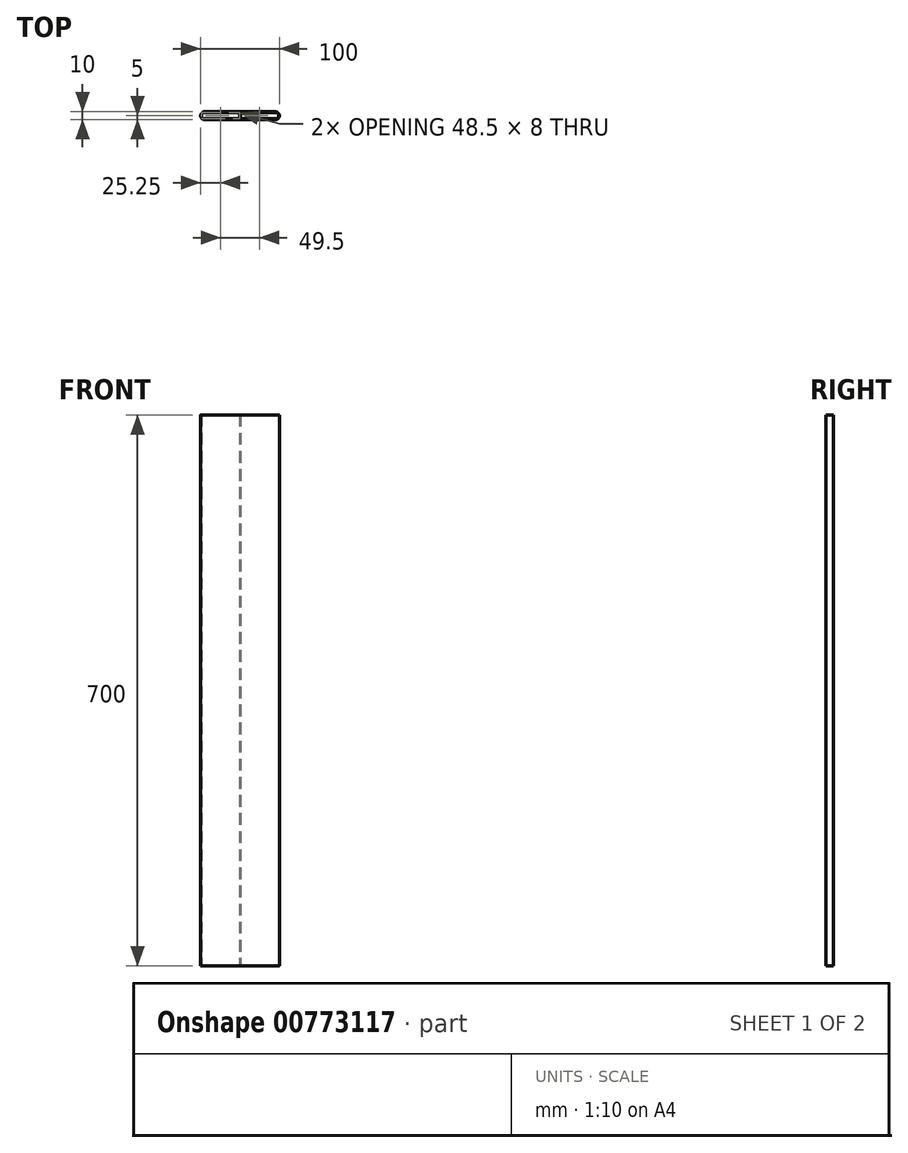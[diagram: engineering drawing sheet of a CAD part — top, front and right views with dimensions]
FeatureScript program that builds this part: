
annotation { "Feature Type Name" : "Feature", "Feature Type Description" : "" }
export const myFeature = defineFeature(function(context is Context, id is Id, definition is map)
    precondition{}
    {
        {
            var Q0;
            Q0=qCreatedBy(makeId("Top.planeOp"),FACE);
            var sketch = newSketch(context, id + "F0", { "sketchPlane" : qUnion([Q0])});
            skLineSegment(sketch, "E0.bottom", {"start": v(-45, 5) * mm, "end": v(45, 5) * mm});
            skLineSegment(sketch, "E0.top", {"start": v(-45, -5) * mm, "end": v(45, -5) * mm});
            skLineSegment(sketch, "E0.left", {"start": v(-50, 0) * mm, "end": v(-50, 0) * mm});
            skLineSegment(sketch, "E0.right", {"start": v(50, 0) * mm, "end": v(50, 0) * mm});
            skPoint(sketch, "E0.middle", {"position": v(0, 0) * mm});
            skPoint(sketch, "E1.visualSharp", {"position": v(-50, 5) * mm});
            skArc(sketch, "E1.filletArc", {"start": v(-45, 5) * mm, "mid": v(-48.54, 3.54) * mm, "end": v(-50, 0) * mm});
            skPoint(sketch, "E2.visualSharp", {"position": v(-50, -5) * mm});
            skArc(sketch, "E2.filletArc", {"start": v(-50, 0) * mm, "mid": v(-48.54, -3.54) * mm, "end": v(-45, -5) * mm});
            skPoint(sketch, "E3.visualSharp", {"position": v(50, 5) * mm});
            skArc(sketch, "E3.filletArc", {"start": v(50, 0) * mm, "mid": v(48.54, 3.54) * mm, "end": v(45, 5) * mm});
            skPoint(sketch, "E4.visualSharp", {"position": v(50, -5) * mm});
            skArc(sketch, "E4.filletArc", {"start": v(45, -5) * mm, "mid": v(48.54, -3.54) * mm, "end": v(50, 0) * mm});
            skLineSegment(sketch, "E5", {"start": v(0, 10.52) * mm, "end": v(0, -13.7) * mm, "construction": true});
            skPoint(sketch, "E5.endSnap0", {"position": v(0, -5) * mm});
            skArc(sketch, "E6.0", {"start": v(-45, 4) * mm, "mid": v(-47.83, 2.83) * mm, "end": v(-49, 0) * mm});
            skArc(sketch, "E6.1", {"start": v(49, 0) * mm, "mid": v(47.83, 2.83) * mm, "end": v(45, 4) * mm});
            skArc(sketch, "E6.2", {"start": v(45, -4) * mm, "mid": v(47.83, -2.83) * mm, "end": v(49, 0) * mm});
            skLineSegment(sketch, "E6.3", {"start": v(-45, 4) * mm, "end": v(-0.5, 4) * mm});
            skLineSegment(sketch, "E6.4", {"start": v(-45, -4) * mm, "end": v(-0.5, -4) * mm});
            skArc(sketch, "E6.5", {"start": v(-49, 0) * mm, "mid": v(-47.83, -2.83) * mm, "end": v(-45, -4) * mm});
            skLineSegment(sketch, "E7", {"start": v(-0.5, 4) * mm, "end": v(-0.5, -4) * mm});
            skLineSegment(sketch, "E8", {"start": v(0.5, 4) * mm, "end": v(0.5, -4) * mm});
            skLineSegment(sketch, "E9.trimOffspring", {"start": v(0.5, 4) * mm, "end": v(45, 4) * mm});
            skLineSegment(sketch, "E10.trimOffspring", {"start": v(0.5, -4) * mm, "end": v(45, -4) * mm});
            skSolve(sketch);
        }
        {
            var Q0;
            Q0 = qSketchRegion(id + "F0", true);
            extrude(context, id + "F1", {"entities" : qUnion([Q0]), "depth" : 700 * mm, "offsetDistance" : 25 * mm});
        }
    });
